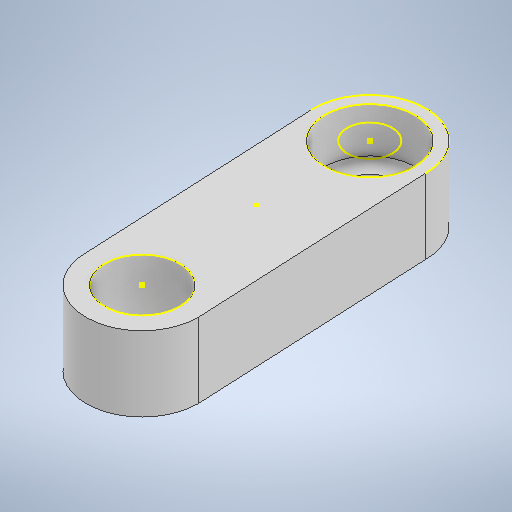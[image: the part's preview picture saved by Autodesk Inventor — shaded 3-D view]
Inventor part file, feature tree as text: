
AUTODESK INVENTOR PART (.ipt)
format: ipt  version: 2025.1 (Build 291241000, 241)  size: 575,488 bytes
history: native  units: in
note: dims shown in document units (in); Inventor stores cm internally (conversion verified against a paired STEP export)
features: sketch x3, extrude x2
ambient origin geometry x8: Origin, YZ Plane, XZ Plane, XY Plane, X Axis, Y Axis, Z Axis, Center Point
bodies: Solid1 (feature_tree)
feature tree (5):
  extrude  "Extrusion1"  Depth=0.1969in
  extrude  "Extrusion2"  Depth=0.1181in
  sketch  "Sketch3"  dims[d4=0.2362in d5=0.1969in d6=0.0in d7=0.2362in d8=0.1181in d9=0.0in d10=0.2953in]
  sketch  "Sketch1"  dims[d0=0.6299in d1=0.1969in]
  sketch  "Sketch2"  dims[d2=0.1181in d3=0.2953in]
